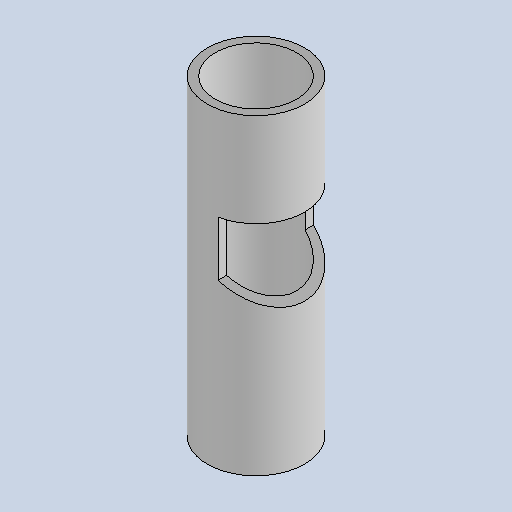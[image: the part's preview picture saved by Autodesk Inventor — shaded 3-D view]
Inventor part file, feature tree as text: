
AUTODESK INVENTOR PART (.ipt)
format: ipt  version: 2025 (Build 290162010, 162A)  size: 152,064 bytes
history: native  units: mm
features: extrude x2, sketch x2, projected_geometry x1
ambient origin geometry x8: Origin, YZ Plane, XZ Plane, XY Plane, X Axis, Y Axis, Z Axis, Center Point
bodies: Solid1 (feature_tree)
feature tree (5):
  extrude  "Extrusion1"  Depth=104.0mm
  extrude  "Extrusion2"  TaperAngle=60.0deg  [1 undecoded]
  sketch  "Sketch1"  dims[d0=125.0mm d1=104.0mm]
  sketch  "Sketch2"  dims[d2=400.0mm d3=0.0mm d4=60.0deg d5=50.0mm d6=120.0mm d7=70.0mm d8=0.0mm d9=0.0mm]
  projected_geometry  "Projected Loop1"
note: 1 required parameter value undecoded (feature->parameter linkage not recoverable at this tier; creation-order binding heuristic only, values carry confidence <= 0.55)
